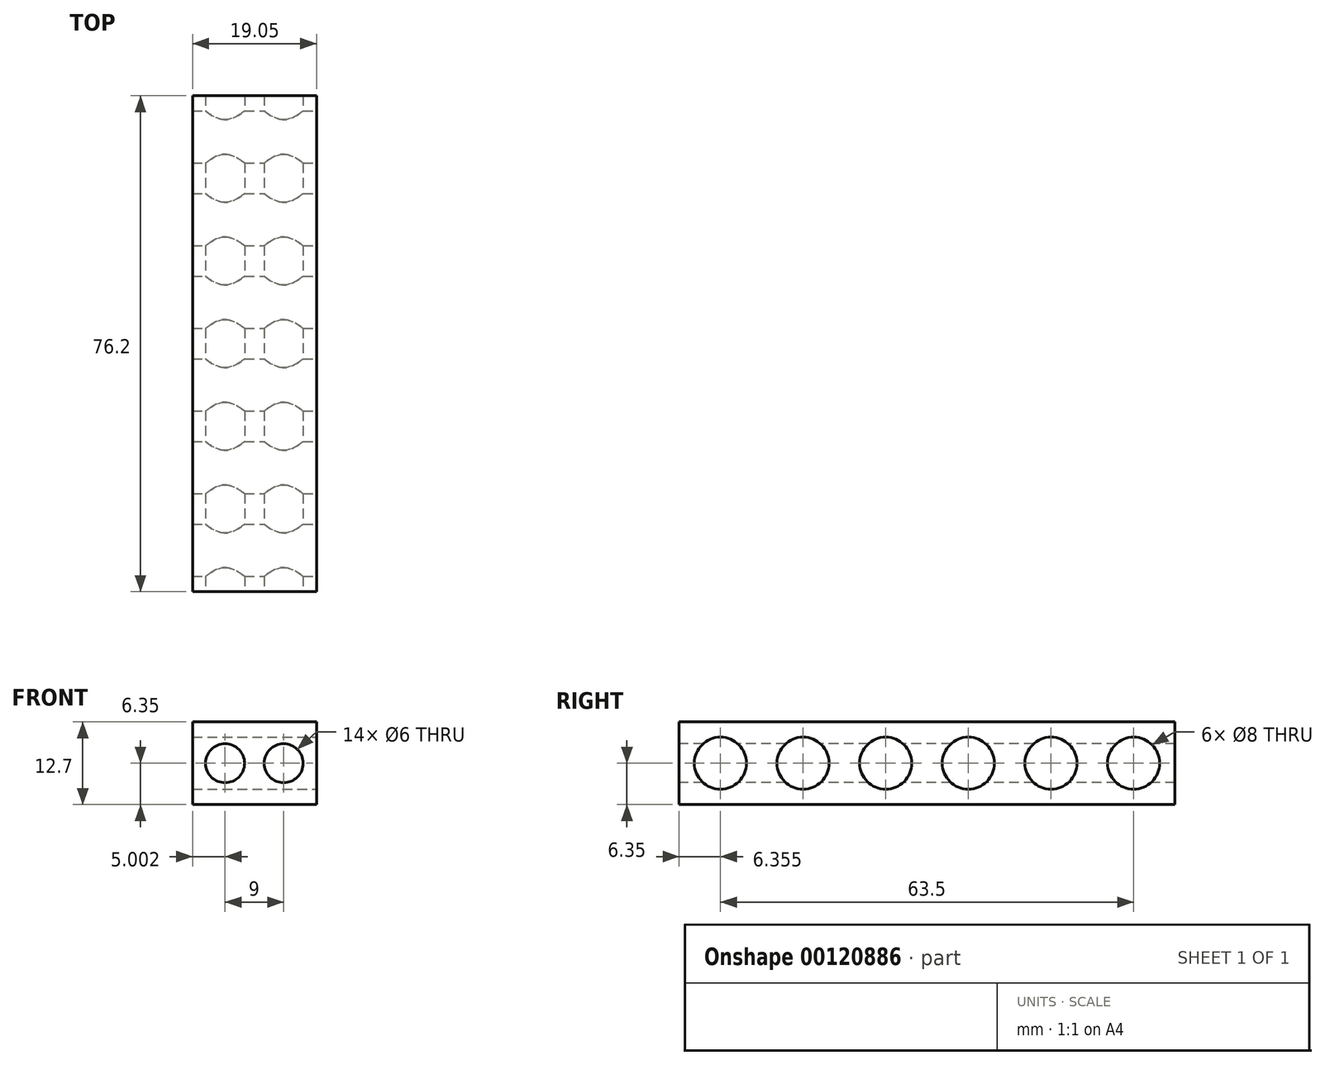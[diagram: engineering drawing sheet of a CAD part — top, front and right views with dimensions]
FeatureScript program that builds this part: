
annotation { "Feature Type Name" : "Feature", "Feature Type Description" : "" }
export const myFeature = defineFeature(function(context is Context, id is Id, definition is map)
    precondition{}
    {
        {
            var Q0;
            Q0=qCreatedBy(makeId("Top.planeOp"),FACE);
            var sketch = newSketch(context, id + "F0", { "sketchPlane" : qUnion([Q0])});
            skLineSegment(sketch, "E0.bottom", {"start": v(-4.64, 52.5) * mm, "end": v(14.41, 52.5) * mm});
            skLineSegment(sketch, "E0.top", {"start": v(-4.64, -23.7) * mm, "end": v(14.41, -23.7) * mm});
            skLineSegment(sketch, "E0.left", {"start": v(-4.64, 52.5) * mm, "end": v(-4.64, -23.7) * mm});
            skLineSegment(sketch, "E0.right", {"start": v(14.41, 52.5) * mm, "end": v(14.41, -23.7) * mm});
            skSolve(sketch);
        }
        {
            var Q0;
            Q0 = qSketchRegion(id + "F0", true);
            extrude(context, id + "F1", {"entities" : qUnion([Q0]), "depth" : 12.7 * mm});
        }
        {
            var Q0;
            Q0=makeQuery(id+"F1.opExtrude","SWEPT_FACE",FACE,{"disambiguationData":[OSD([sQuery(id+"F0.wireOp",EDGE,"E0.right")])]});
            var sketch = newSketch(context, id + "F2", { "sketchPlane" : qUnion([Q0])});
            skCircle(sketch, "E1", {"center": v(-17.35, 6.35) * mm, "radius": 4 * mm});
            skCircle(sketch, "E2.1.0.0", {"center": v(-4.65, 6.35) * mm, "radius": 4 * mm});
            skCircle(sketch, "E2.2.0.0", {"center": v(8.05, 6.35) * mm, "radius": 4 * mm});
            skCircle(sketch, "E2.3.0.0", {"center": v(20.75, 6.35) * mm, "radius": 4 * mm});
            skCircle(sketch, "E2.4.0.0", {"center": v(33.45, 6.35) * mm, "radius": 4 * mm});
            skCircle(sketch, "E2.5.0.0", {"center": v(46.15, 6.35) * mm, "radius": 4 * mm});
            skLineSegment(sketch, "E2.direction1", {"start": v(-17.35, 6.35) * mm, "end": v(-4.65, 6.35) * mm, "construction": true});
            skSolve(sketch);
        }
        {
            var Q0;
            Q0 = qSketchRegion(id + "F2", true);
            extrude(context, id + "F3", {"entities" : qUnion([Q0]), "operationType" : NewBodyOperationType.REMOVE, "endBound" : BoundingType.THROUGH_ALL, "oppositeDirection" : true, "depth" : 25 * mm});
        }
        {
            var Q0;
            Q0=makeQuery(id+"F1.opExtrude","SWEPT_FACE",FACE,{"disambiguationData":[OSD([sQuery(id+"F0.wireOp",EDGE,"E0.top")])]});
            var sketch = newSketch(context, id + "F4", { "sketchPlane" : qUnion([Q0])});
            skCircle(sketch, "E3", {"center": v(0.36, 6.35) * mm, "radius": 3 * mm});
            skCircle(sketch, "E4", {"center": v(9.36, 6.35) * mm, "radius": 3 * mm});
            skLineSegment(sketch, "E5", {"start": v(-4.64, 0) * mm, "end": v(14.41, 0) * mm});
            skSolve(sketch);
        }
        {
            var Q0;
            Q0 = qSketchRegion(id + "F4", true);
            extrude(context, id + "F5", {"entities" : qUnion([Q0]), "operationType" : NewBodyOperationType.REMOVE, "endBound" : BoundingType.THROUGH_ALL, "oppositeDirection" : true, "depth" : 25 * mm});
        }
    });
